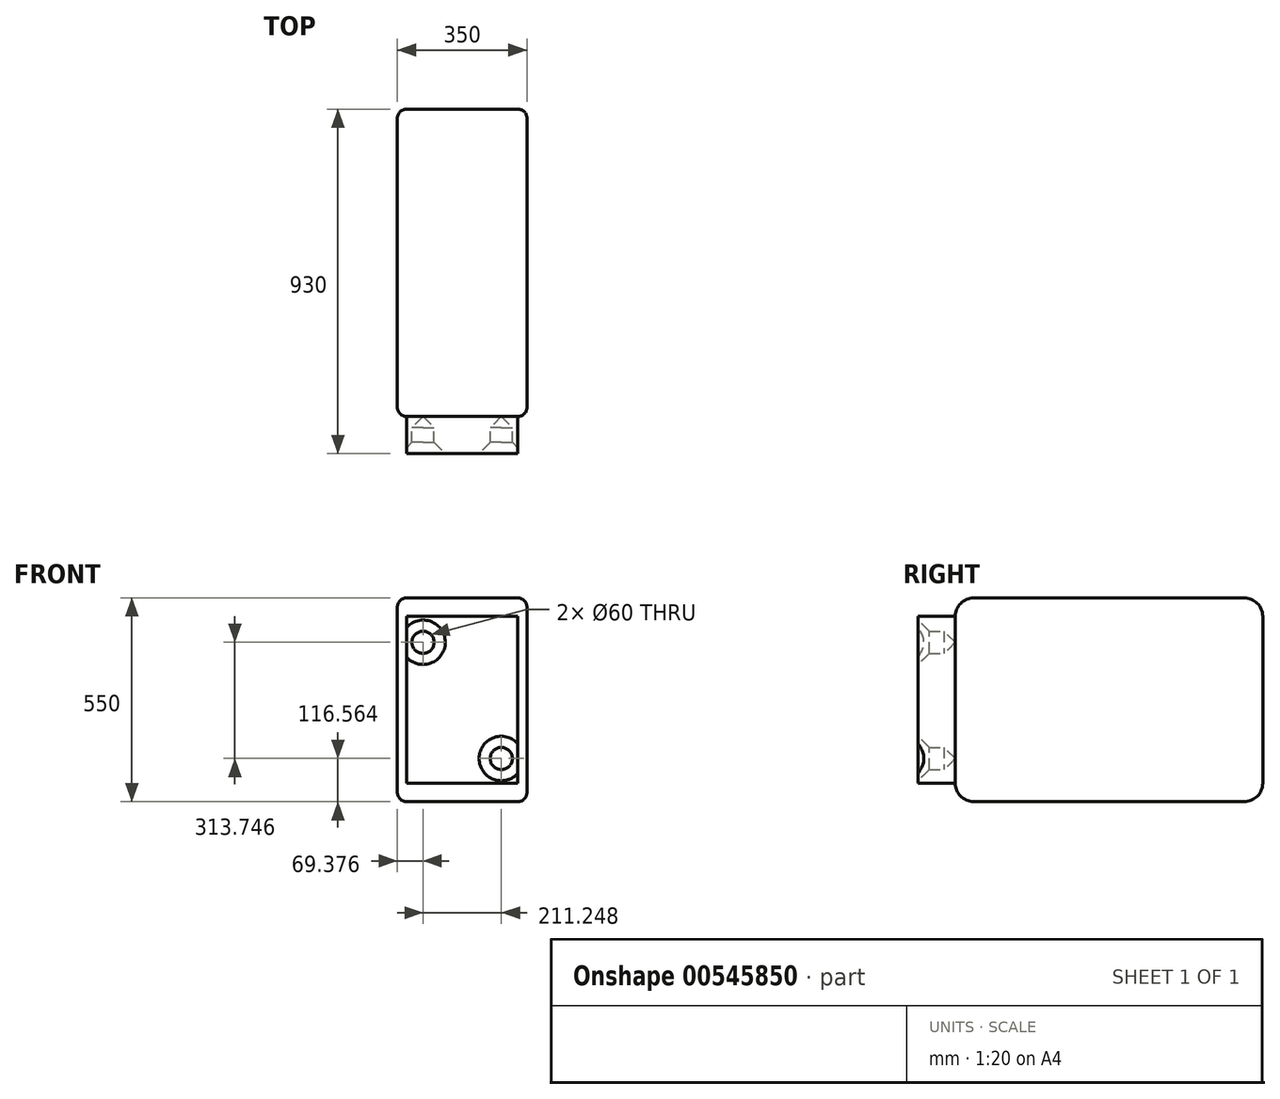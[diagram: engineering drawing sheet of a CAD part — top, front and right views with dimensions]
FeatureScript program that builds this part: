
annotation { "Feature Type Name" : "Feature", "Feature Type Description" : "" }
export const myFeature = defineFeature(function(context is Context, id is Id, definition is map)
    precondition{}
    {
        {
            var Q0;
            Q0=qCreatedBy(makeId("Top.planeOp"),FACE);
            var sketch = newSketch(context, id + "F0", { "sketchPlane" : qUnion([Q0])});
            skLineSegment(sketch, "E0", {"start": v(0, 0) * mm, "end": v(0, -1700) * mm, "construction": true});
            skLineSegment(sketch, "E1", {"start": v(0, -1700) * mm, "end": v(-425, -1700) * mm, "construction": true});
            skLineSegment(sketch, "E2", {"start": v(-675, 0) * mm, "end": v(0, 0) * mm, "construction": true});
            skLineSegment(sketch, "E3", {"start": v(-675, -1200) * mm, "end": v(-675, -1700) * mm, "construction": true});
            skLineSegment(sketch, "E4", {"start": v(-675, -1700) * mm, "end": v(-425, -1700) * mm, "construction": true});
            skLineSegment(sketch, "E5.MirrorCS", {"start": v(675, 0) * mm, "end": v(0, 0) * mm, "construction": true});
            skLineSegment(sketch, "E6.MirrorCS", {"start": v(0, -1700) * mm, "end": v(425, -1700) * mm, "construction": true});
            skLineSegment(sketch, "E7", {"start": v(-425, -1700) * mm, "end": v(-675, -1200) * mm, "construction": true});
            skLineSegment(sketch, "E8", {"start": v(675, 0) * mm, "end": v(675, -1200) * mm, "construction": true});
            skLineSegment(sketch, "E9", {"start": v(425, -1700) * mm, "end": v(-425, -1700) * mm});
            skLineSegment(sketch, "E10", {"start": v(675, -1200) * mm, "end": v(425, -1700) * mm, "construction": true});
            skLineSegment(sketch, "E11", {"start": v(-675, -1200) * mm, "end": v(-675, 0) * mm, "construction": true});
            skLineSegment(sketch, "E12", {"start": v(-425, -650) * mm, "end": v(0, -650) * mm, "construction": true});
            skLineSegment(sketch, "E13.MirrorCS", {"start": v(425, -650) * mm, "end": v(0, -650) * mm, "construction": true});
            skLineSegment(sketch, "E14", {"start": v(-425, -650) * mm, "end": v(-425, -1700) * mm, "construction": true});
            skLineSegment(sketch, "E15", {"start": v(425, -650) * mm, "end": v(425, -1700) * mm, "construction": true});
            skLineSegment(sketch, "E16", {"start": v(-675, -1200) * mm, "end": v(-675, -1700) * mm});
            skLineSegment(sketch, "E17", {"start": v(-425, -1700) * mm, "end": v(-425, -1200) * mm});
            skLineSegment(sketch, "E18", {"start": v(-425, -1200) * mm, "end": v(-675, -1200) * mm});
            skLineSegment(sketch, "E19.MirrorCS", {"start": v(425, -1200) * mm, "end": v(675, -1200) * mm});
            skLineSegment(sketch, "E20.MirrorCS", {"start": v(425, -1700) * mm, "end": v(425, -1200) * mm});
            skLineSegment(sketch, "E21.MirrorCS", {"start": v(675, -1700) * mm, "end": v(425, -1700) * mm, "construction": true});
            skLineSegment(sketch, "E22.MirrorCS", {"start": v(675, -1200) * mm, "end": v(675, -1700) * mm, "construction": true});
            skLineSegment(sketch, "E23", {"start": v(-380, -800) * mm, "end": v(-380, -1630) * mm});
            skLineSegment(sketch, "E24", {"start": v(-30, -800) * mm, "end": v(-30, -1630) * mm});
            skLineSegment(sketch, "E25", {"start": v(-380, -800) * mm, "end": v(-30, -800) * mm});
            skLineSegment(sketch, "E26", {"start": v(-380, -1630) * mm, "end": v(-30, -1630) * mm});
            skSolve(sketch);
        }
        {
            var Q0;
            Q0 = qSketchRegion(id + "F0", true);
            extrude(context, id + "F1", {"entities" : qUnion([Q0]), "depth" : 550 * mm, "offsetDistance" : 25 * mm});
        }
        {
            var Q0;
            Q0=makeQuery(id+"F1.opExtrude","CAP_EDGE",EDGE,{"disambiguationData":[OSD([sQuery(id+"F0.wireOp",EDGE,"E26")])],"isStart":false});
            var Q1;
            Q1=makeQuery(id+"F1.opExtrude","CAP_EDGE",EDGE,{"disambiguationData":[OSD([sQuery(id+"F0.wireOp",EDGE,"E25")])],"isStart":false});
            var Q2;
            Q2=makeQuery(id+"F1.opExtrude","CAP_EDGE",EDGE,{"disambiguationData":[OSD([sQuery(id+"F0.wireOp",EDGE,"E25")])],"isStart":true});
            var Q3;
            Q3=makeQuery(id+"F1.opExtrude","CAP_EDGE",EDGE,{"disambiguationData":[OSD([sQuery(id+"F0.wireOp",EDGE,"E26")])],"isStart":true});
            fillet(context, id + "F2", {"entities" : qUnion([Q0, Q1, Q2, Q3]), "radius" : 50 * mm, "tangentPropagation" : true, "allowEdgeOverflow" : false});
        }
        {
            var Q0;
            Q0=makeQuery(id+"F1.opExtrude","SWEPT_FACE",FACE,{"disambiguationData":[OSD([sQuery(id+"F0.wireOp",EDGE,"E24")])]});
            fillet(context, id + "F3", {"entities" : qUnion([Q0]), "radius" : 25 * mm, "tangentPropagation" : true, "allowEdgeOverflow" : false});
        }
        {
            var Q0;
            Q0=makeQuery(id+"F1.opExtrude","SWEPT_FACE",FACE,{"disambiguationData":[OSD([sQuery(id+"F0.wireOp",EDGE,"E23")])]});
            fillet(context, id + "F4", {"entities" : qUnion([Q0]), "radius" : 25 * mm, "tangentPropagation" : true, "allowEdgeOverflow" : false});
        }
        {
            var Q0;
            Q0=makeQuery(id+"F1.opExtrude","SWEPT_FACE",FACE,{"disambiguationData":[OSD([sQuery(id+"F0.wireOp",EDGE,"E26")])]});
            var sketch = newSketch(context, id + "F5", { "sketchPlane" : qUnion([Q0])});
            skLineSegment(sketch, "E27.bottom", {"start": v(-355, 500) * mm, "end": v(-55, 500) * mm});
            skLineSegment(sketch, "E27.top", {"start": v(-355, 50) * mm, "end": v(-55, 50) * mm});
            skLineSegment(sketch, "E27.left", {"start": v(-355, 500) * mm, "end": v(-355, 50) * mm});
            skLineSegment(sketch, "E27.right", {"start": v(-55, 500) * mm, "end": v(-55, 50) * mm});
            skCircle(sketch, "E28", {"center": v(-310.62, 116.56) * mm, "radius": 30 * mm});
            skLineSegment(sketch, "E29", {"start": v(-205, 413.45) * mm, "end": v(-205, -906.5) * mm, "construction": true});
            skPoint(sketch, "E29.endSnap0", {"position": v(-205, 275) * mm});
            skLineSegment(sketch, "E30", {"start": v(-288.67, 273.44) * mm, "end": v(-101.14, 273.44) * mm, "construction": true});
            skCircle(sketch, "E31.MirrorC", {"center": v(-310.62, 430.3) * mm, "radius": 30 * mm});
            skCircle(sketch, "E32.MirrorC", {"center": v(-99.38, 430.3) * mm, "radius": 30 * mm});
            skCircle(sketch, "E33.MirrorC", {"center": v(-99.38, 116.56) * mm, "radius": 30 * mm});
            skSolve(sketch);
        }
        {
            var Q0;
            Q0=makeQuery(id+"F5.imprint","IMPRINT",FACE,{"disambiguationData":[TD([[makeQuery(id+"F5.imprint","IMPRINT",EDGE,{"derivedFrom":sQuery(id+"F5.wireOp",EDGE,"E28")}),1.0]])]});
            var Q1;
            Q1=makeQuery(id+"F5.imprint","IMPRINT",FACE,{"disambiguationData":[TD([[makeQuery(id+"F5.imprint","IMPRINT",EDGE,{"derivedFrom":sQuery(id+"F5.wireOp",EDGE,"E31.MirrorC")}),-1.0]])]});
            var Q2;
            Q2=makeQuery(id+"F5.imprint","IMPRINT",FACE,{"disambiguationData":[TD([[makeQuery(id+"F5.imprint","IMPRINT",EDGE,{"derivedFrom":sQuery(id+"F5.wireOp",EDGE,"E32.MirrorC")}),1.0]])]});
            var Q3;
            Q3=makeQuery(id+"F5.imprint","IMPRINT",FACE,{"disambiguationData":[TD([[makeQuery(id+"F5.imprint","IMPRINT",EDGE,{"derivedFrom":sQuery(id+"F5.wireOp",EDGE,"E33.MirrorC")}),-1.0]])]});
            extrude(context, id + "F6", {"entities" : qUnion([Q0, Q1, Q2, Q3]), "operationType" : NewBodyOperationType.ADD, "depth" : 100 * mm, "offsetDistance" : 25 * mm});
        }
        {
            var Q0;
            Q0=makeQuery(id+"F6.opExtrude","CAP_EDGE",EDGE,{"disambiguationData":[OSD([sQuery(id+"F5.wireOp",EDGE,"E28")])],"isStart":false});
            var Q1;
            Q1=makeQuery(id+"F6.opExtrude","SWEPT_FACE",FACE,{"disambiguationData":[OSD([sQuery(id+"F5.wireOp",EDGE,"E28")])]});
            var Q2;
            Q2=makeQuery(id+"F6.opExtrude","SWEPT_FACE",FACE,{"disambiguationData":[OSD([sQuery(id+"F5.wireOp",EDGE,"E31.MirrorC")])]});
            var Q3;
            Q3=makeQuery(id+"F6.opExtrude","SWEPT_FACE",FACE,{"disambiguationData":[OSD([sQuery(id+"F5.wireOp",EDGE,"E32.MirrorC")])]});
            var Q4;
            Q4=makeQuery(id+"F6.opExtrude","SWEPT_FACE",FACE,{"disambiguationData":[OSD([sQuery(id+"F5.wireOp",EDGE,"E33.MirrorC")])]});
            chamfer(context, id + "F7", {"entities" : qUnion([Q0, Q1, Q2, Q3, Q4]), "width" : 30 * mm, "tangentPropagation" : true});
        }
    });
